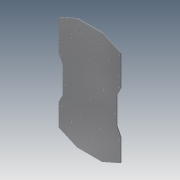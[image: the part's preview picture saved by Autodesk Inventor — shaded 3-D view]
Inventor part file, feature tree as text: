
AUTODESK INVENTOR PART (.ipt)
format: ipt  version: 2013 (Build 170138000, 138)  size: 150,528 bytes
history: native  units: mm
features: extrude x1, sketch x1
ambient origin geometry x8: Origin, YZ Plane, XZ Plane, XY Plane, X Axis, Y Axis, Z Axis, Center Point
bodies: Solid1 (feature_tree)
feature tree (2):
  extrude  "Extrusion1"  Depth=4.0mm
  sketch  "Sketch1"  dims[d0=4.0mm d1=4.0mm d2=4.0mm d3=4.0mm d4=4.0mm d5=4.0mm d6=4.0mm d7=4.0mm d8=4.0mm d9=4.0mm d10=4.0mm d11=4.0mm d12=4.0mm d13=4.0mm d14=4.0mm d15=4.0mm d16=4.0mm d17=4.0mm d18=4.0mm d19=4.0mm d20=4.0mm d21=4.0mm d22=4.0mm d23=4.0mm d24=4.0mm d25=2.0mm d26=0.0mm]
